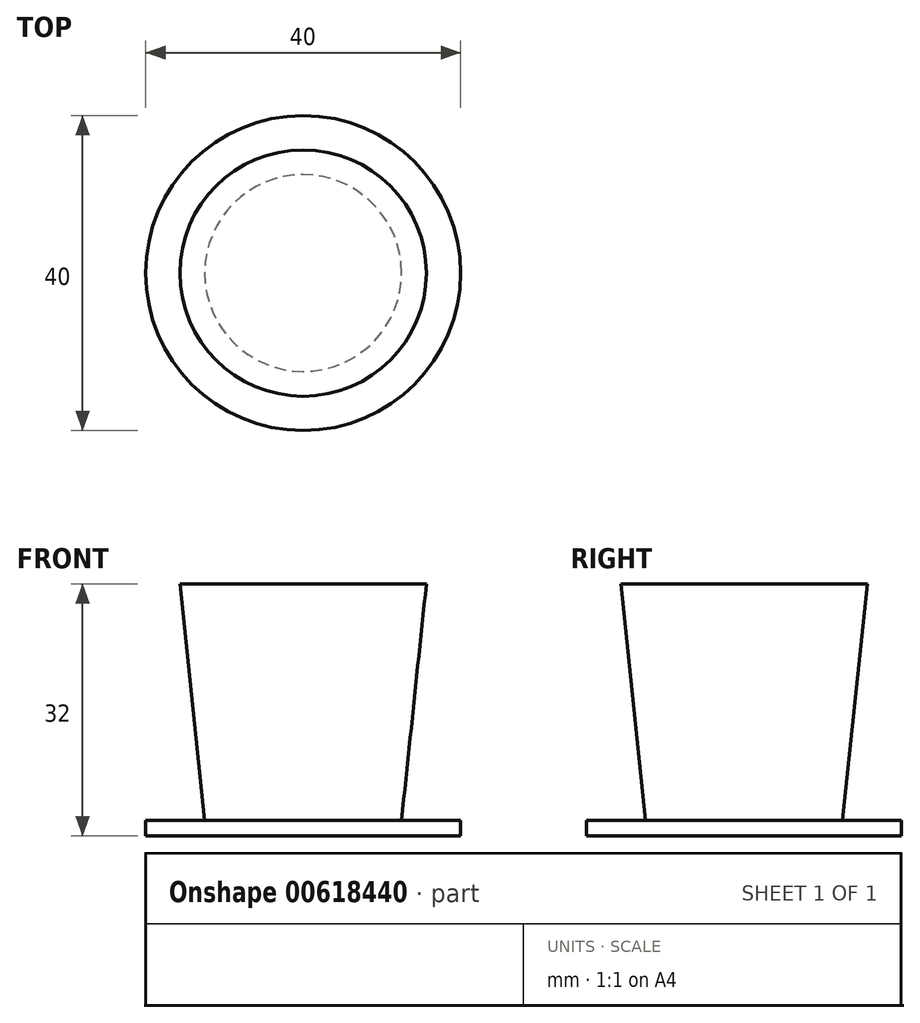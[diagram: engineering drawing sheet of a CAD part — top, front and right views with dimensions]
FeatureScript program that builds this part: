
annotation { "Feature Type Name" : "Feature", "Feature Type Description" : "" }
export const myFeature = defineFeature(function(context is Context, id is Id, definition is map)
    precondition{}
    {
        {
            var Q0;
            Q0=qCreatedBy(makeId("Top.planeOp"),FACE);
            var sketch = newSketch(context, id + "F0", { "sketchPlane" : qUnion([Q0])});
            skCircle(sketch, "E0", {"center": v(0, 0) * mm, "radius": 20 * mm});
            skSolve(sketch);
        }
        {
            var Q0;
            Q0=makeQuery(id+"F0.imprint","IMPRINT",FACE,{"disambiguationData":[TD([[makeQuery(id+"F0.imprint","IMPRINT",EDGE,{"derivedFrom":sQuery(id+"F0.wireOp",EDGE,"E0")}),1.0]])]});
            extrude(context, id + "F1", {"entities" : qUnion([Q0]), "depth" : 2 * mm, "offsetDistance" : 25 * mm});
        }
        {
            var Q0;
            Q0=makeQuery(id+"F1.opExtrude","CAP_FACE",FACE,{"disambiguationData":[OSD([sQuery(id+"F0.wireOp",EDGE,"E0")])],"isStart":false});
            var sketch = newSketch(context, id + "F2", { "sketchPlane" : qUnion([Q0])});
            skCircle(sketch, "E1", {"center": v(0, 0) * mm, "radius": 12.5 * mm});
            skSolve(sketch);
        }
        {
            var Q0;
            Q0=makeQuery(id+"F2.imprint","IMPRINT",FACE,{"disambiguationData":[TD([[makeQuery(id+"F2.imprint","IMPRINT",EDGE,{"derivedFrom":sQuery(id+"F2.wireOp",EDGE,"E1")}),1.0]])]});
            extrude(context, id + "F3", {"entities" : qUnion([Q0]), "operationType" : NewBodyOperationType.ADD, "depth" : 30 * mm, "offsetDistance" : 25 * mm, "hasDraft" : true, "draftAngle" : 6 * degree});
        }
    });
